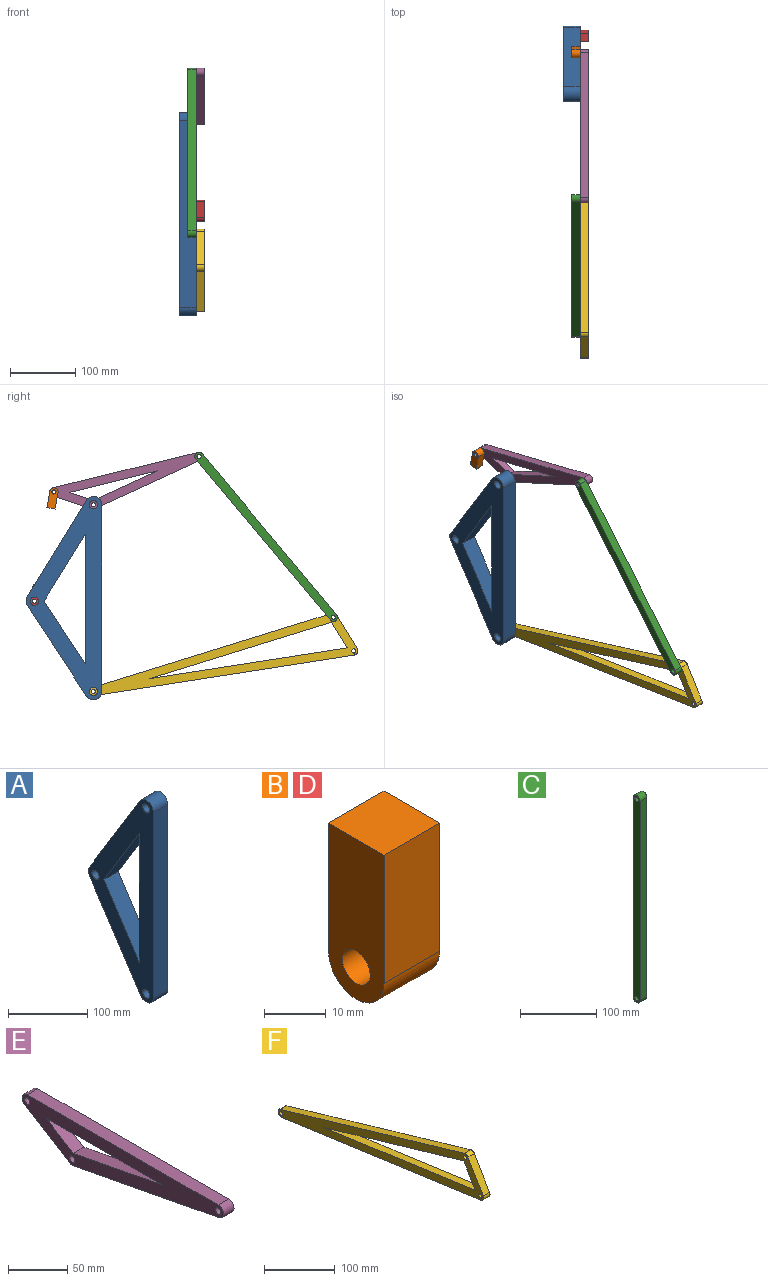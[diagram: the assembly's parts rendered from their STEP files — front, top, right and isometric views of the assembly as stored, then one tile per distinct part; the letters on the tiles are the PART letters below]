
ASSEMBLY  parts=6 mates=7
PART A: 14 faces, bbox 25.4x115.8x311.2 mm
  f0: plane 138.18x90.36mm, normal (0,0.84,-0.55), area 4193.5mm2, adj f9,f10,f11,f13
  f1: plane 147.57x90.36mm, normal (0,0.85,0.52), area 4395.2mm2, adj f9,f10,f11,f12
  f2: plane 102.29x62.63mm, normal (0,-0.85,-0.52), area 3046.4mm2, adj f3,f7,f9,f10
  f3: plane 95.78x62.63mm, normal (0,-0.84,0.55), area 2906.7mm2, adj f2,f7,f9,f10
  f4: cylinder r=6.35mm len=25.4mm, axis (-1,0,0), area 1013.4mm2, adj f9,f10
  f5: cylinder r=6.35mm len=25.4mm, axis (-1,0,0), area 1013.4mm2, adj f9,f10
  f6: cylinder r=6.35mm len=25.4mm, axis (-1,0,0), area 1013.4mm2, adj f9,f10
  f7: plane 198.06x25.4mm, normal (0,1,0), area 5030.8mm2, adj f2,f3,f9,f10
  f8: plane 285.75x25.4mm, normal (0,-1,0), area 7258mm2, adj f9,f10,f12,f13
  f9: plane 311.15x115.76mm, normal (1,0,0), area 14757.7mm2, adj f0,f1,f2,f3,f4,f5,f6,f7
  f10: plane 311.15x115.76mm, normal (-1,0,0), area 14757.7mm2, adj f0,f1,f2,f3,f4,f5,f6,f7
  f11: cylinder r=12.7mm len=25.4mm, axis (-1,0,0), area 364mm2, adj f0,f1,f9,f10
  f12: cylinder r=12.7mm len=25.4mm, axis (-1,0,0), area 836.2mm2, adj f1,f8,f9,f10
  f13: cylinder r=12.7mm len=25.4mm, axis (-1,0,0), area 826.6mm2, adj f0,f8,f9,f10
PART B: 7 faces, bbox 12.7x12.7x31.8 mm
  f0: plane 12.7x12.7mm, normal (0,0,1), area 161.3mm2, adj f1,f3,f5,f6
  f1: plane 25.4x12.7mm, normal (0,-1,0), area 322.6mm2, adj f0,f2,f5,f6
  f2: cylinder r=6.35mm len=12.7mm, axis (-1,0,0), area 253.4mm2, adj f1,f3,f5,f6
  f3: plane 25.4x12.7mm, normal (0,1,0), area 322.6mm2, adj f0,f2,f5,f6
  f4: cylinder r=3.17mm len=12.7mm, axis (-1,0,0), area 253.4mm2, adj f5,f6
  f5: plane 31.75x12.7mm, normal (1,0,0), area 354.2mm2, adj f0,f1,f2,f3,f4
  f6: plane 31.75x12.7mm, normal (-1,0,0), area 354.2mm2, adj f0,f1,f2,f3,f4
PART C: 8 faces, bbox 12.7x12.7x333.4 mm
  f0: plane 320.68x12.7mm, normal (0,-1,0), area 4072.6mm2, adj f1,f4,f6,f7
  f1: cylinder r=6.35mm len=12.7mm, axis (-1,0,0), area 253.4mm2, adj f0,f2,f6,f7
  f2: plane 320.68x12.7mm, normal (0,1,0), area 4072.6mm2, adj f1,f4,f6,f7
  f3: cylinder r=3.17mm len=12.7mm, axis (-1,0,0), area 253.4mm2, adj f6,f7
  f4: cylinder r=6.35mm len=12.7mm, axis (-1,0,0), area 253.4mm2, adj f0,f2,f6,f7
  f5: cylinder r=3.17mm len=12.7mm, axis (-1,0,0), area 253.4mm2, adj f6,f7
  f6: plane 333.38x12.7mm, normal (1,0,0), area 4135.9mm2, adj f0,f1,f2,f3,f4,f5
  f7: plane 333.38x12.7mm, normal (-1,0,0), area 4135.9mm2, adj f0,f1,f2,f3,f4,f5
PART D: same geometry as B
PART E: 14 faces, bbox 12.7x241.3x46.2 mm
  f0: plane 174.63x33.45mm, normal (0,-0.19,-0.98), area 2258.1mm2, adj f9,f10,f11,f13
  f1: plane 53.98x33.45mm, normal (0,0.53,-0.85), area 806.5mm2, adj f9,f10,f11,f12
  f2: plane 106.48x20.4mm, normal (0,0.19,0.98), area 1376.9mm2, adj f3,f4,f9,f10
  f3: plane 139.4x12.7mm, normal (0,0,-1), area 1770.4mm2, adj f2,f4,f9,f10
  f4: plane 32.91x20.4mm, normal (0,-0.53,0.85), area 491.8mm2, adj f2,f3,f9,f10
  f5: cylinder r=3.17mm len=12.7mm, axis (-1,0,0), area 253.4mm2, adj f9,f10
  f6: cylinder r=3.17mm len=12.7mm, axis (-1,0,0), area 253.4mm2, adj f9,f10
  f7: cylinder r=3.17mm len=12.7mm, axis (-1,0,0), area 253.4mm2, adj f9,f10
  f8: plane 228.6x12.7mm, normal (0,0,1), area 2903.2mm2, adj f9,f10,f12,f13
  f9: plane 241.3x46.15mm, normal (1,0,0), area 5417.2mm2, adj f0,f1,f2,f3,f4,f5,f6,f7
  f10: plane 241.3x46.15mm, normal (-1,0,0), area 5417.2mm2, adj f0,f1,f2,f3,f4,f5,f6,f7
  f11: cylinder r=6.35mm len=12.7mm, axis (-1,0,0), area 60mm2, adj f0,f1,f9,f10
  f12: cylinder r=6.35mm len=12.7mm, axis (-1,0,0), area 208.6mm2, adj f1,f8,f9,f10
  f13: cylinder r=6.35mm len=12.7mm, axis (-1,0,0), area 238.1mm2, adj f0,f8,f9,f10
PART F: 14 faces, bbox 12.7x412x120.8 mm
  f0: plane 303.64x42.67mm, normal (0,0.14,0.99), area 3894.1mm2, adj f1,f8,f9,f10
  f1: plane 39.51x23.3mm, normal (0,0.86,-0.51), area 582.6mm2, adj f0,f8,f9,f10
  f2: plane 399.3x56.11mm, normal (0,-0.14,-0.99), area 5121mm2, adj f9,f10,f11,f13
  f3: plane 368.66x108.07mm, normal (0,0.28,0.96), area 4879mm2, adj f9,f10,f11,f12
  f4: cylinder r=3.17mm len=12.7mm, axis (-1,0,0), area 253.4mm2, adj f9,f10
  f5: cylinder r=3.17mm len=12.7mm, axis (-1,0,0), area 253.4mm2, adj f9,f10
  f6: cylinder r=3.17mm len=12.7mm, axis (-1,0,0), area 253.4mm2, adj f9,f10
  f7: plane 51.96x30.64mm, normal (0,-0.86,0.51), area 766.1mm2, adj f9,f10,f12,f13
  f8: plane 280.34x82.18mm, normal (0,-0.28,-0.96), area 3710.1mm2, adj f0,f1,f9,f10
  f9: plane 412x120.77mm, normal (1,0,0), area 10152.9mm2, adj f0,f1,f2,f3,f4,f5,f6,f7
  f10: plane 412x120.77mm, normal (-1,0,0), area 10152.9mm2, adj f0,f1,f2,f3,f4,f5,f6,f7
  f11: cylinder r=6.35mm len=12.7mm, axis (-1,0,0), area 241.6mm2, adj f2,f3,f9,f10
  f12: cylinder r=6.35mm len=12.7mm, axis (-1,0,0), area 106.7mm2, adj f3,f7,f9,f10
  f13: cylinder r=6.35mm len=12.7mm, axis (-1,0,0), area 158.4mm2, adj f2,f7,f9,f10
PLACE A at identity fixed
PLACE B rot(axis=(-1,0,0),169.8deg) t=(12.7,60.39,305.38)mm
PLACE C rot(axis=(-1,0,0),39.8deg) t=(12.7,-367,113.57)mm
PLACE D rot(axis=(1,0,0),10.2deg) t=(25.4,90.36,138.18)mm
PLACE E rot(axis=(-1,0,0),13.8deg) t=(25.4,0,285.75)mm
PLACE F rot(axis=(-1,0,0),0.9deg) t=(25.4,0,0)mm
MATE revolute D.f4 <-> A.f4  axis (-1,0,0) through (25.4,90.36,138.18)mm
MATE slider B.f0 <-> D.f0  axis (0,0.18,-0.98) through (25.4,64.87,280.38)mm
MATE revolute A.f6 <-> E.f7  axis (1,0,0) through (25.4,0,285.75)mm
MATE revolute C.f3 <-> F.f5  axis (-1,0,0) through (25.4,-367,113.57)mm
MATE revolute B.f4 <-> E.f6  axis (1,0,0) through (25.4,60.39,305.38)mm
MATE revolute F.f4 <-> A.f5  axis (-1,0,0) through (25.4,0,0)mm
MATE revolute C.f4 <-> E.f5  axis (-1,0,0) through (25.4,-161.63,359.85)mm
